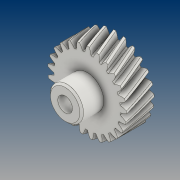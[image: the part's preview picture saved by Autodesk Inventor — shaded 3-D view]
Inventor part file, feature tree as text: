
AUTODESK INVENTOR PART (.ipt)
format: ipt  version: 2021 (Build 250183000, 183)  size: 523,776 bytes
history: native  units: mm (DEFAULTED — no unit token found)
features: extrude x3, plane x3, other x3, sketch x3, chamfer x1
ambient origin geometry x8: Origin, YZ Plane, XZ Plane, XY Plane, X Axis, Y Axis, Z Axis, Center Point
bodies: Solid1 (feature_tree)
feature tree (13):
  extrude  "Extrusion1"  Depth=15.0mm TaperAngle=0.0deg
  plane  "Work Plane2"
  plane  "Work Plane8"
  plane  "Work Plane9"
  other  "Spur Gear"
  sketch  "Sketch3"  dims[d16=60.0mm d17=0.0mm d34=1.256637mm d39=0.0mm d41=0.0mm d43=60.0mm d46=60.0mm d47=0.0mm d48=0.0mm d49=5.0mm d50=8.0mm d51=0.0mm d52=0.0mm d53=12.0mm d54=0.0mm d55=1.0mm d56=2.0mm d57=45.0deg]
  extrude  "Extrusion2"  Depth=10.0mm TaperAngle=0.0deg
  extrude  "Extrusion3"  Depth=1.256637mm TaperAngle=0.0deg
  chamfer  "Chamfer1"  [1 undecoded]
  sketch  "Sketch1"  dims[d0=42.9045mm d1=15.0mm d2=0.0mm]
  sketch  "Sketch2"  dims[d3=39.906666mm d4=10.0mm d5=0.0mm]
  other  "Srf1"
  other  "Pitch Diameter"
note: 1 required parameter value undecoded (feature->parameter linkage not recoverable at this tier; creation-order binding heuristic only, values carry confidence <= 0.55)
